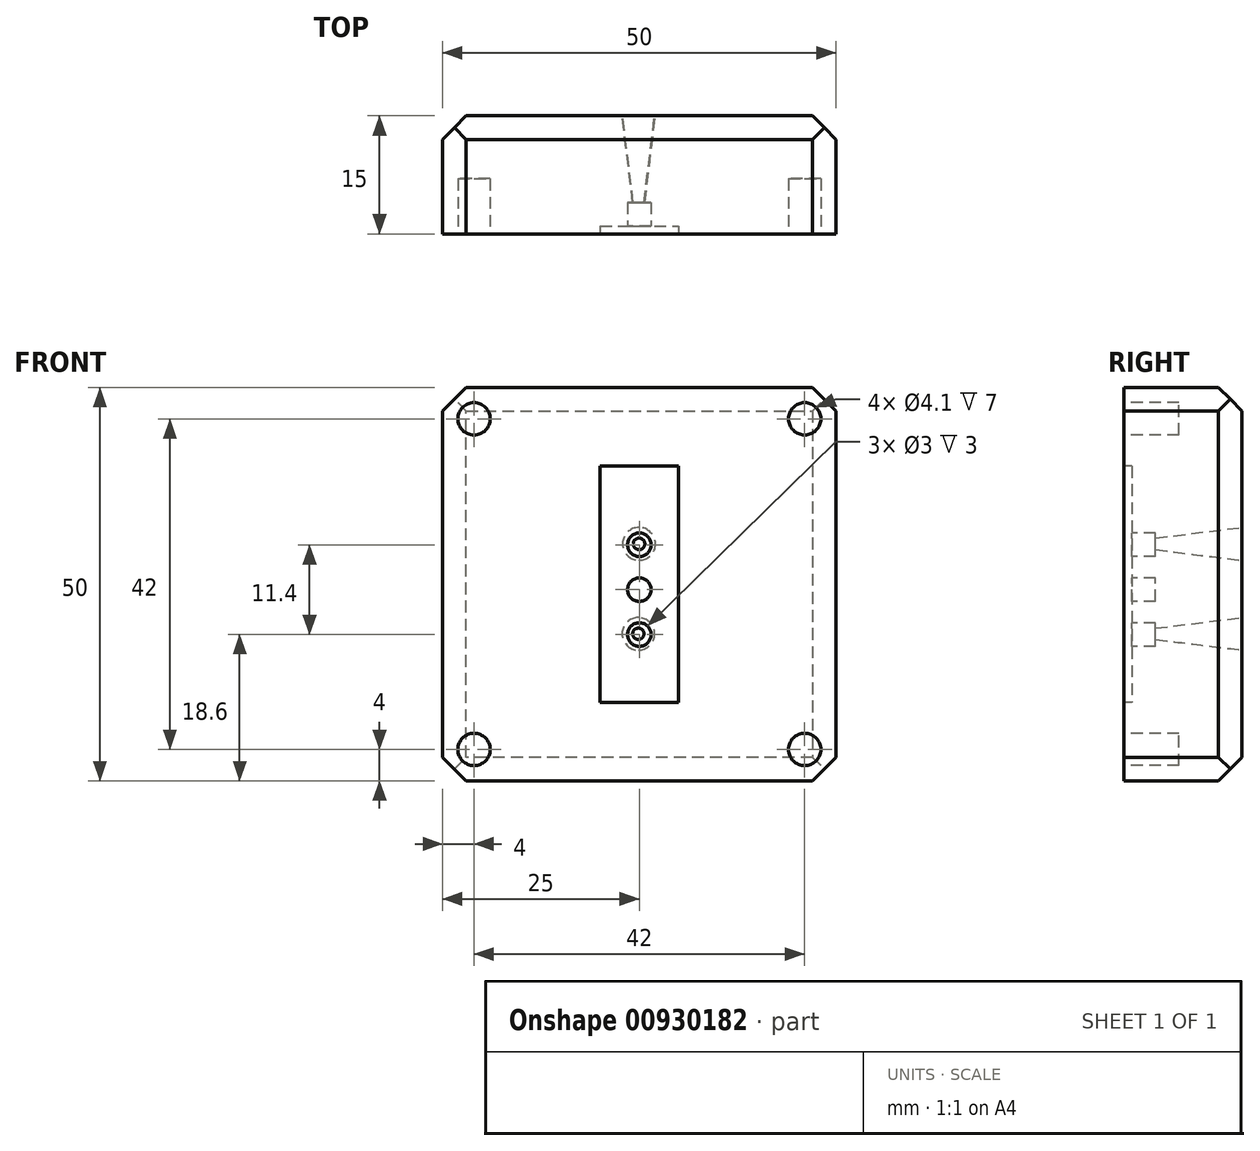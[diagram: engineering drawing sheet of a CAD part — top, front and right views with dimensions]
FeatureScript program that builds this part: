
annotation { "Feature Type Name" : "Feature", "Feature Type Description" : "" }
export const myFeature = defineFeature(function(context is Context, id is Id, definition is map)
    precondition{}
    {
        {
            var Q0;
            Q0=qCreatedBy(makeId("Front.planeOp"),FACE);
            var sketch = newSketch(context, id + "F0", { "sketchPlane" : qUnion([Q0])});
            skLineSegment(sketch, "E0.bottom", {"start": v(0, 0) * mm, "end": v(50, 0) * mm});
            skLineSegment(sketch, "E0.top", {"start": v(0, 50) * mm, "end": v(50, 50) * mm});
            skLineSegment(sketch, "E0.left", {"start": v(0, 0) * mm, "end": v(0, 50) * mm});
            skLineSegment(sketch, "E0.right", {"start": v(50, 0) * mm, "end": v(50, 50) * mm});
            skSolve(sketch);
        }
        {
            var Q0;
            Q0=makeQuery(id+"F0.imprint","IMPRINT",FACE,{"disambiguationData":[TD([[makeQuery(id+"F0.imprint","IMPRINT",EDGE,{"derivedFrom":sQuery(id+"F0.wireOp",EDGE,"E0.bottom")}),1.0]])]});
            extrude(context, id + "F1", {"entities" : qUnion([Q0]), "depth" : 15 * mm, "offsetDistance" : 25 * mm});
        }
        {
            var Q0;
            Q0=makeQuery(id+"F1.opExtrude","CAP_FACE",FACE,{"disambiguationData":[OSD([sQuery(id+"F0.wireOp",EDGE,"E0.bottom"),sQuery(id+"F0.wireOp",EDGE,"E0.top"),sQuery(id+"F0.wireOp",EDGE,"E0.left"),sQuery(id+"F0.wireOp",EDGE,"E0.right")])],"isStart":false});
            var sketch = newSketch(context, id + "F2", { "sketchPlane" : qUnion([Q0])});
            skLineSegment(sketch, "E1.bottom", {"start": v(20, 40) * mm, "end": v(30, 40) * mm});
            skLineSegment(sketch, "E1.top", {"start": v(20, 10) * mm, "end": v(30, 10) * mm});
            skLineSegment(sketch, "E1.left", {"start": v(20, 40) * mm, "end": v(20, 10) * mm});
            skLineSegment(sketch, "E1.right", {"start": v(30, 40) * mm, "end": v(30, 10) * mm});
            skSolve(sketch);
        }
        {
            var Q0;
            Q0=makeQuery(id+"F2.imprint","IMPRINT",FACE,{"disambiguationData":[TD([[makeQuery(id+"F2.imprint","IMPRINT",EDGE,{"derivedFrom":sQuery(id+"F2.wireOp",EDGE,"E1.bottom")}),-1.0]])]});
            extrude(context, id + "F3", {"entities" : qUnion([Q0]), "operationType" : NewBodyOperationType.REMOVE, "oppositeDirection" : true, "depth" : 1 * mm, "offsetDistance" : 25 * mm});
        }
        {
            var Q0;
            Q0=makeQuery(id+"F2.imprint","IMPRINT",FACE,{"disambiguationData":[TD([[makeQuery(id+"F2.imprint","IMPRINT",EDGE,{"derivedFrom":sQuery(id+"F2.wireOp",EDGE,"E1.bottom")}),1.0]])]});
            var sketch = newSketch(context, id + "F4", { "sketchPlane" : qUnion([Q0])});
            skLineSegment(sketch, "E2", {"start": v(25, 0) * mm, "end": v(25, 49.27) * mm, "construction": true});
            skSolve(sketch);
        }
        {
            var Q0;
            Q0=makeQuery(id+"F2.imprint","IMPRINT",FACE,{"disambiguationData":[TD([[makeQuery(id+"F2.imprint","IMPRINT",EDGE,{"derivedFrom":sQuery(id+"F2.wireOp",EDGE,"E1.bottom")}),1.0]])]});
            var sketch = newSketch(context, id + "F5", { "sketchPlane" : qUnion([Q0])});
            skCircle(sketch, "E3", {"center": v(25, 30) * mm, "radius": 1.5 * mm});
            skCircle(sketch, "E4.1.0.0", {"center": v(25, 24.3) * mm, "radius": 1.5 * mm});
            skCircle(sketch, "E4.2.0.0", {"center": v(25, 18.6) * mm, "radius": 1.5 * mm});
            skLineSegment(sketch, "E4.direction1", {"start": v(25, 30) * mm, "end": v(25, 24.3) * mm, "construction": true});
            skSolve(sketch);
        }
        {
            var Q0;
            Q0 = qSketchRegion(id + "F5", true);
            extrude(context, id + "F6", {"entities" : qUnion([Q0]), "operationType" : NewBodyOperationType.REMOVE, "oppositeDirection" : true, "depth" : 4 * mm, "offsetDistance" : 25 * mm});
        }
        {
            var Q0;
            Q0=makeQuery(id+"F4.imprint","IMPRINT",FACE,{"disambiguationData":[TD([[makeQuery(id+"F4.imprint","IMPRINT",EDGE,{"derivedFrom":makeQuery(id+"F2.imprint","IMPRINT",EDGE,{"derivedFrom":sQuery(id+"F2.wireOp",EDGE,"E1.bottom")})}),1.0]])]});
            var sketch = newSketch(context, id + "F7", { "sketchPlane" : qUnion([Q0])});
            skCircle(sketch, "E5", {"center": v(46, 46) * mm, "radius": 2.05 * mm});
            skCircle(sketch, "E6", {"center": v(46, 4) * mm, "radius": 2.05 * mm});
            skCircle(sketch, "E7", {"center": v(4, 4) * mm, "radius": 2.05 * mm});
            skCircle(sketch, "E8", {"center": v(4, 46) * mm, "radius": 2.05 * mm});
            skSolve(sketch);
        }
        {
            var Q0;
            Q0 = qSketchRegion(id + "F7", true);
            extrude(context, id + "F8", {"entities" : qUnion([Q0]), "operationType" : NewBodyOperationType.REMOVE, "oppositeDirection" : true, "depth" : 7 * mm, "offsetDistance" : 25 * mm});
        }
        {
            var Q0;
            Q0=makeQuery(id+"F1.opExtrude","CAP_FACE",FACE,{"disambiguationData":[OSD([sQuery(id+"F0.wireOp",EDGE,"E0.bottom"),sQuery(id+"F0.wireOp",EDGE,"E0.top"),sQuery(id+"F0.wireOp",EDGE,"E0.left"),sQuery(id+"F0.wireOp",EDGE,"E0.right")])],"isStart":true});
            chamfer(context, id + "F9", {"entities" : qUnion([Q0]), "width" : 3 * mm, "tangentPropagation" : true});
        }
        {
            var Q0;
            Q0=makeQuery(id+"F1.opExtrude","SWEPT_EDGE",EDGE,{"disambiguationData":[OSD([sQuery(id+"F0.wireOp",EDGE,"E0.top"),sQuery(id+"F0.wireOp",EDGE,"E0.left")])]});
            var Q1;
            Q1=makeQuery(id+"F1.opExtrude","SWEPT_EDGE",EDGE,{"disambiguationData":[OSD([sQuery(id+"F0.wireOp",EDGE,"E0.top"),sQuery(id+"F0.wireOp",EDGE,"E0.right")])]});
            var Q2;
            Q2=makeQuery(id+"F1.opExtrude","SWEPT_EDGE",EDGE,{"disambiguationData":[OSD([sQuery(id+"F0.wireOp",EDGE,"E0.bottom"),sQuery(id+"F0.wireOp",EDGE,"E0.right")])]});
            var Q3;
            Q3=makeQuery(id+"F1.opExtrude","SWEPT_EDGE",EDGE,{"disambiguationData":[OSD([sQuery(id+"F0.wireOp",EDGE,"E0.bottom"),sQuery(id+"F0.wireOp",EDGE,"E0.left")])]});
            chamfer(context, id + "F10", {"entities" : qUnion([Q0, Q1, Q2, Q3]), "width" : 3 * mm, "tangentPropagation" : true});
        }
        {
            var Q0;
            Q0=makeQuery(id+"F1.opExtrude","CAP_FACE",FACE,{"disambiguationData":[OSD([sQuery(id+"F0.wireOp",EDGE,"E0.bottom"),sQuery(id+"F0.wireOp",EDGE,"E0.top"),sQuery(id+"F0.wireOp",EDGE,"E0.left"),sQuery(id+"F0.wireOp",EDGE,"E0.right")])],"isStart":true});
            var sketch = newSketch(context, id + "F11", { "sketchPlane" : qUnion([Q0])});
            skCircle(sketch, "E9", {"center": v(-24.96, 30.11) * mm, "radius": 2.09 * mm});
            skCircle(sketch, "E10", {"center": v(-24.87, 18.7) * mm, "radius": 2.07 * mm});
            skSolve(sketch);
        }
        {
            var Q0;
            Q0=makeQuery(id+"F11.imprint","IMPRINT",FACE,{"disambiguationData":[TD([[makeQuery(id+"F11.imprint","IMPRINT",EDGE,{"derivedFrom":sQuery(id+"F11.wireOp",EDGE,"E9")}),1.0]])]});
            var Q1;
            Q1=makeQuery(id+"F11.imprint","IMPRINT",FACE,{"disambiguationData":[TD([[makeQuery(id+"F11.imprint","IMPRINT",EDGE,{"derivedFrom":sQuery(id+"F11.wireOp",EDGE,"E10")}),1.0]])]});
            extrude(context, id + "F12", {"entities" : qUnion([Q0, Q1]), "operationType" : NewBodyOperationType.REMOVE, "oppositeDirection" : true, "depth" : 12 * mm, "offsetDistance" : 25 * mm, "hasDraft" : true, "draftAngle" : 7 * degree, "draftPullDirection" : true});
        }
    });
